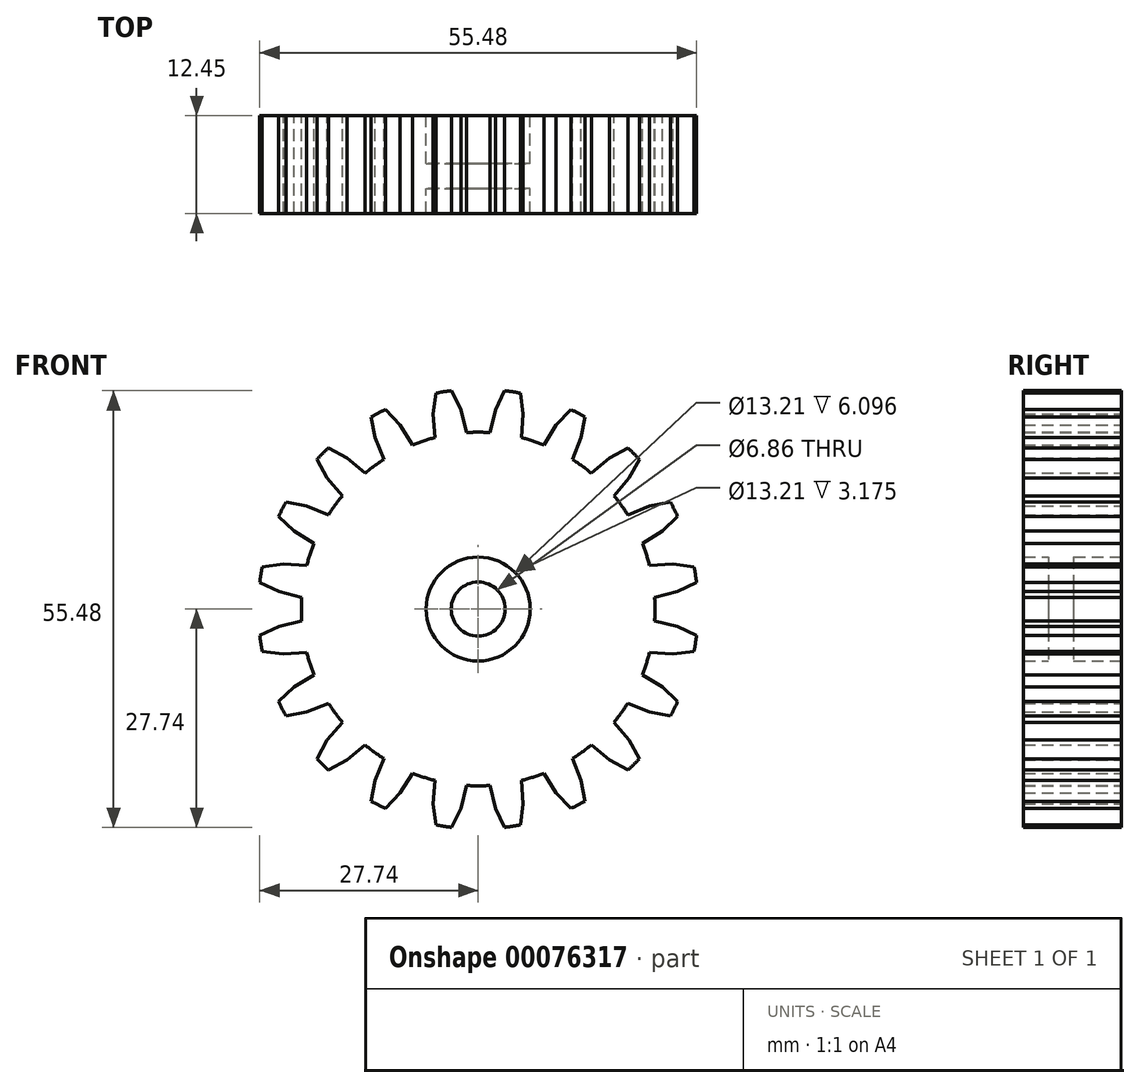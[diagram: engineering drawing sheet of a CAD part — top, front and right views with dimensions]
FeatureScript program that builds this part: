
annotation { "Feature Type Name" : "Feature", "Feature Type Description" : "" }
export const myFeature = defineFeature(function(context is Context, id is Id, definition is map)
    precondition{}
    {
        {
            var Q0;
            Q0=qCreatedBy(makeId("Top.planeOp"),FACE);
            var sketch = newSketch(context, id + "F0", { "sketchPlane" : qUnion([Q0])});
            skLineSegment(sketch, "E0", {"start": v(0, 6.35) * mm, "end": v(0, -6.35) * mm});
            skLineSegment(sketch, "E1", {"start": v(6.6, 6.35) * mm, "end": v(6.6, -6.35) * mm});
            skLineSegment(sketch, "E2", {"start": v(6.6, -6.35) * mm, "end": v(50.8, -6.35) * mm});
            skLineSegment(sketch, "E3", {"start": v(50.8, -6.35) * mm, "end": v(50.8, 6.35) * mm});
            skLineSegment(sketch, "E4", {"start": v(50.8, 6.35) * mm, "end": v(6.6, 6.35) * mm});
            skLineSegment(sketch, "E5", {"start": v(6.6, 0) * mm, "end": v(3.43, 0) * mm});
            skLineSegment(sketch, "E6", {"start": v(3.43, 0) * mm, "end": v(3.43, -3.18) * mm});
            skLineSegment(sketch, "E7", {"start": v(3.43, -3.18) * mm, "end": v(6.6, -3.18) * mm});
            skSolve(sketch);
        }
        {
            var Q0;
            Q0=makeQuery(id+"F0.imprint","IMPRINT",FACE,{"disambiguationData":[TD([[makeQuery(id+"F0.imprint","IMPRINT",EDGE,{"derivedFrom":sQuery(id+"F0.wireOp",EDGE,"3r0X1BRl-RbRB-vlo6-oPl6-QrHitKXkx0XH")}),1.0]])]});
            var Q1;
            Q1=makeQuery(id+"F0.imprint","IMPRINT",FACE,{"disambiguationData":[TD([[makeQuery(id+"F0.imprint","IMPRINT",EDGE,{"derivedFrom":sQuery(id+"F0.wireOp",EDGE,"E1")}),1.0]])]});
            var Q2;
            {var subQ4=sQuery(id+"F0.wireOp",EDGE,"VTUfDxQO-eAQO-8rXd-4OAK-vWdJqYTGuIOz");Q2=makeQuery(id+"F0.imprint","IMPRINT",FACE,{"disambiguationData":[TD([[makeQuery(id+"F0.imprint","IMPRINT",EDGE,{"derivedFrom":subQ4}),1.0]])]});}
            var Q3;
            {var subQ0=sQuery(id+"F0.wireOp",EDGE,"E5");Q3=makeQuery(id+"F0.imprint","IMPRINT",FACE,{"disambiguationData":[TD([[makeQuery(id+"F0.imprint","IMPRINT",EDGE,{"derivedFrom":subQ0}),1.0]])]});}
            var Q4;
            Q4=sQuery(id+"F0.wireOp",EDGE,"E0");
            revolve(context, id + "F1", {"entities" : qUnion([Q0, Q1, Q2, Q3]), "axis" : qUnion([Q4]), "revolveType" : RevolveType.FULL});
        }
        {
            var Q0;
            Q0=makeQuery(id+"F1.opRevolve","SWEPT_FACE",FACE,{"disambiguationData":[OSD([sQuery(id+"F0.wireOp",EDGE,"E4")])]});
            var sketch = newSketch(context, id + "F2", { "sketchPlane" : qUnion([Q0])});
            skCircle(sketch, "E8.0", {"center": v(0, 0) * mm, "radius": 50.8 * mm, "construction": true});
            skCircle(sketch, "E9", {"center": v(76.2, 0) * mm, "radius": 25.4 * mm, "construction": true});
            skCircle(sketch, "E10", {"center": v(0, 0) * mm, "radius": 53.34 * mm, "construction": true});
            skCircle(sketch, "E11", {"center": v(0, 0) * mm, "radius": 47.86 * mm, "construction": true});
            skLineSegment(sketch, "E12", {"start": v(-2.03, 47.82) * mm, "end": v(-1.78, 50.77) * mm});
            skLineSegment(sketch, "E13", {"start": v(-1.78, 50.77) * mm, "end": v(-1.02, 53.33) * mm});
            skLineSegment(sketch, "E14", {"start": v(2.03, 47.82) * mm, "end": v(1.78, 50.77) * mm});
            skLineSegment(sketch, "E15", {"start": v(1.78, 50.77) * mm, "end": v(1.02, 53.33) * mm});
            skCircle(sketch, "E16", {"center": v(76.2, 0) * mm, "radius": 27.94 * mm, "construction": true});
            skCircle(sketch, "E17", {"center": v(76.2, 0) * mm, "radius": 22.46 * mm, "construction": true});
            skLineSegment(sketch, "E18.1.0", {"start": v(-5.47, 47.55) * mm, "end": v(-6.19, 50.42) * mm});
            skLineSegment(sketch, "E18.1.1", {"start": v(-9.49, 46.91) * mm, "end": v(-9.7, 49.87) * mm});
            skLineSegment(sketch, "E18.1.2", {"start": v(-9.7, 49.87) * mm, "end": v(-9.35, 52.51) * mm});
            skLineSegment(sketch, "E18.1.3", {"start": v(-6.19, 50.42) * mm, "end": v(-7.34, 52.83) * mm});
            skLineSegment(sketch, "E18.2.0", {"start": v(-12.84, 46.1) * mm, "end": v(-14, 48.83) * mm});
            skLineSegment(sketch, "E18.2.1", {"start": v(-16.7, 44.85) * mm, "end": v(-17.38, 47.73) * mm});
            skLineSegment(sketch, "E18.2.2", {"start": v(-17.38, 47.73) * mm, "end": v(-17.45, 50.4) * mm});
            skLineSegment(sketch, "E18.2.3", {"start": v(-14, 48.83) * mm, "end": v(-15.51, 51.03) * mm});
            skLineSegment(sketch, "E18.3.0", {"start": v(-19.9, 43.53) * mm, "end": v(-21.46, 46.04) * mm});
            skLineSegment(sketch, "E18.3.1", {"start": v(-23.52, 41.68) * mm, "end": v(-24.63, 44.43) * mm});
            skLineSegment(sketch, "E18.3.2", {"start": v(-24.63, 44.43) * mm, "end": v(-25.12, 47.06) * mm});
            skLineSegment(sketch, "E18.3.3", {"start": v(-21.46, 46.04) * mm, "end": v(-23.3, 47.98) * mm});
            skLineSegment(sketch, "E18.4.0", {"start": v(-26.46, 39.88) * mm, "end": v(-28.4, 42.12) * mm});
            skLineSegment(sketch, "E18.4.1", {"start": v(-29.75, 37.5) * mm, "end": v(-31.28, 40.03) * mm});
            skLineSegment(sketch, "E18.4.2", {"start": v(-31.28, 40.03) * mm, "end": v(-32.17, 42.55) * mm});
            skLineSegment(sketch, "E18.4.3", {"start": v(-28.4, 42.12) * mm, "end": v(-30.52, 43.74) * mm});
            skLineSegment(sketch, "E18.5.0", {"start": v(-32.38, 35.25) * mm, "end": v(-34.64, 37.16) * mm});
            skLineSegment(sketch, "E18.5.1", {"start": v(-35.25, 32.38) * mm, "end": v(-37.16, 34.64) * mm});
            skLineSegment(sketch, "E18.5.2", {"start": v(-37.16, 34.64) * mm, "end": v(-38.43, 37) * mm});
            skLineSegment(sketch, "E18.5.3", {"start": v(-34.64, 37.16) * mm, "end": v(-37, 38.43) * mm});
            skLineSegment(sketch, "E18.6.0", {"start": v(-37.5, 29.75) * mm, "end": v(-40.03, 31.28) * mm});
            skLineSegment(sketch, "E18.6.1", {"start": v(-39.88, 26.46) * mm, "end": v(-42.12, 28.4) * mm});
            skLineSegment(sketch, "E18.6.2", {"start": v(-42.12, 28.4) * mm, "end": v(-43.74, 30.52) * mm});
            skLineSegment(sketch, "E18.6.3", {"start": v(-40.03, 31.28) * mm, "end": v(-42.55, 32.17) * mm});
            skLineSegment(sketch, "E18.7.0", {"start": v(-41.68, 23.52) * mm, "end": v(-44.43, 24.63) * mm});
            skLineSegment(sketch, "E18.7.1", {"start": v(-43.53, 19.9) * mm, "end": v(-46.04, 21.46) * mm});
            skLineSegment(sketch, "E18.7.2", {"start": v(-46.04, 21.46) * mm, "end": v(-47.98, 23.3) * mm});
            skLineSegment(sketch, "E18.7.3", {"start": v(-44.43, 24.63) * mm, "end": v(-47.06, 25.12) * mm});
            skLineSegment(sketch, "E18.8.0", {"start": v(-44.85, 16.7) * mm, "end": v(-47.73, 17.38) * mm});
            skLineSegment(sketch, "E18.8.1", {"start": v(-46.1, 12.84) * mm, "end": v(-48.83, 14) * mm});
            skLineSegment(sketch, "E18.8.2", {"start": v(-48.83, 14) * mm, "end": v(-51.03, 15.51) * mm});
            skLineSegment(sketch, "E18.8.3", {"start": v(-47.73, 17.38) * mm, "end": v(-50.4, 17.45) * mm});
            skLineSegment(sketch, "E18.9.0", {"start": v(-46.91, 9.49) * mm, "end": v(-49.87, 9.7) * mm});
            skLineSegment(sketch, "E18.9.1", {"start": v(-47.55, 5.47) * mm, "end": v(-50.42, 6.19) * mm});
            skLineSegment(sketch, "E18.9.2", {"start": v(-50.42, 6.19) * mm, "end": v(-52.83, 7.34) * mm});
            skLineSegment(sketch, "E18.9.3", {"start": v(-49.87, 9.7) * mm, "end": v(-52.51, 9.35) * mm});
            skLineSegment(sketch, "E18.10.0", {"start": v(-47.82, 2.03) * mm, "end": v(-50.77, 1.78) * mm});
            skLineSegment(sketch, "E18.10.1", {"start": v(-47.82, -2.03) * mm, "end": v(-50.77, -1.78) * mm});
            skLineSegment(sketch, "E18.10.2", {"start": v(-50.77, -1.78) * mm, "end": v(-53.33, -1.02) * mm});
            skLineSegment(sketch, "E18.10.3", {"start": v(-50.77, 1.78) * mm, "end": v(-53.33, 1.02) * mm});
            skLineSegment(sketch, "E18.11.0", {"start": v(-47.55, -5.47) * mm, "end": v(-50.42, -6.19) * mm});
            skLineSegment(sketch, "E18.11.1", {"start": v(-46.91, -9.49) * mm, "end": v(-49.87, -9.7) * mm});
            skLineSegment(sketch, "E18.11.2", {"start": v(-49.87, -9.7) * mm, "end": v(-52.51, -9.35) * mm});
            skLineSegment(sketch, "E18.11.3", {"start": v(-50.42, -6.19) * mm, "end": v(-52.83, -7.34) * mm});
            skLineSegment(sketch, "E18.12.0", {"start": v(-46.1, -12.84) * mm, "end": v(-48.83, -14) * mm});
            skLineSegment(sketch, "E18.12.1", {"start": v(-44.85, -16.7) * mm, "end": v(-47.73, -17.38) * mm});
            skLineSegment(sketch, "E18.12.2", {"start": v(-47.73, -17.38) * mm, "end": v(-50.4, -17.45) * mm});
            skLineSegment(sketch, "E18.12.3", {"start": v(-48.83, -14) * mm, "end": v(-51.03, -15.51) * mm});
            skLineSegment(sketch, "E18.13.0", {"start": v(-43.53, -19.9) * mm, "end": v(-46.04, -21.46) * mm});
            skLineSegment(sketch, "E18.13.1", {"start": v(-41.68, -23.52) * mm, "end": v(-44.43, -24.63) * mm});
            skLineSegment(sketch, "E18.13.2", {"start": v(-44.43, -24.63) * mm, "end": v(-47.06, -25.12) * mm});
            skLineSegment(sketch, "E18.13.3", {"start": v(-46.04, -21.46) * mm, "end": v(-47.98, -23.3) * mm});
            skLineSegment(sketch, "E18.14.0", {"start": v(-39.88, -26.46) * mm, "end": v(-42.12, -28.4) * mm});
            skLineSegment(sketch, "E18.14.1", {"start": v(-37.5, -29.75) * mm, "end": v(-40.03, -31.28) * mm});
            skLineSegment(sketch, "E18.14.2", {"start": v(-40.03, -31.28) * mm, "end": v(-42.55, -32.17) * mm});
            skLineSegment(sketch, "E18.14.3", {"start": v(-42.12, -28.4) * mm, "end": v(-43.74, -30.52) * mm});
            skLineSegment(sketch, "E18.15.0", {"start": v(-35.25, -32.38) * mm, "end": v(-37.16, -34.64) * mm});
            skLineSegment(sketch, "E18.15.1", {"start": v(-32.38, -35.25) * mm, "end": v(-34.64, -37.16) * mm});
            skLineSegment(sketch, "E18.15.2", {"start": v(-34.64, -37.16) * mm, "end": v(-37, -38.43) * mm});
            skLineSegment(sketch, "E18.15.3", {"start": v(-37.16, -34.64) * mm, "end": v(-38.43, -37) * mm});
            skLineSegment(sketch, "E18.16.0", {"start": v(-29.75, -37.5) * mm, "end": v(-31.28, -40.03) * mm});
            skLineSegment(sketch, "E18.16.1", {"start": v(-26.46, -39.88) * mm, "end": v(-28.4, -42.12) * mm});
            skLineSegment(sketch, "E18.16.2", {"start": v(-28.4, -42.12) * mm, "end": v(-30.52, -43.74) * mm});
            skLineSegment(sketch, "E18.16.3", {"start": v(-31.28, -40.03) * mm, "end": v(-32.17, -42.55) * mm});
            skLineSegment(sketch, "E18.17.0", {"start": v(-23.52, -41.68) * mm, "end": v(-24.63, -44.43) * mm});
            skLineSegment(sketch, "E18.17.1", {"start": v(-19.9, -43.53) * mm, "end": v(-21.46, -46.04) * mm});
            skLineSegment(sketch, "E18.17.2", {"start": v(-21.46, -46.04) * mm, "end": v(-23.3, -47.98) * mm});
            skLineSegment(sketch, "E18.17.3", {"start": v(-24.63, -44.43) * mm, "end": v(-25.12, -47.06) * mm});
            skLineSegment(sketch, "E18.18.0", {"start": v(-16.7, -44.85) * mm, "end": v(-17.38, -47.73) * mm});
            skLineSegment(sketch, "E18.18.1", {"start": v(-12.84, -46.1) * mm, "end": v(-14, -48.83) * mm});
            skLineSegment(sketch, "E18.18.2", {"start": v(-14, -48.83) * mm, "end": v(-15.51, -51.03) * mm});
            skLineSegment(sketch, "E18.18.3", {"start": v(-17.38, -47.73) * mm, "end": v(-17.45, -50.4) * mm});
            skLineSegment(sketch, "E18.19.0", {"start": v(-9.49, -46.91) * mm, "end": v(-9.7, -49.87) * mm});
            skLineSegment(sketch, "E18.19.1", {"start": v(-5.47, -47.55) * mm, "end": v(-6.19, -50.42) * mm});
            skLineSegment(sketch, "E18.19.2", {"start": v(-6.19, -50.42) * mm, "end": v(-7.34, -52.83) * mm});
            skLineSegment(sketch, "E18.19.3", {"start": v(-9.7, -49.87) * mm, "end": v(-9.35, -52.51) * mm});
            skLineSegment(sketch, "E18.20.0", {"start": v(-2.03, -47.82) * mm, "end": v(-1.78, -50.77) * mm});
            skLineSegment(sketch, "E18.20.1", {"start": v(2.03, -47.82) * mm, "end": v(1.78, -50.77) * mm});
            skLineSegment(sketch, "E18.20.2", {"start": v(1.78, -50.77) * mm, "end": v(1.02, -53.33) * mm});
            skLineSegment(sketch, "E18.20.3", {"start": v(-1.78, -50.77) * mm, "end": v(-1.02, -53.33) * mm});
            skLineSegment(sketch, "E18.21.0", {"start": v(5.47, -47.55) * mm, "end": v(6.19, -50.42) * mm});
            skLineSegment(sketch, "E18.21.1", {"start": v(9.49, -46.91) * mm, "end": v(9.7, -49.87) * mm});
            skLineSegment(sketch, "E18.21.2", {"start": v(9.7, -49.87) * mm, "end": v(9.35, -52.51) * mm});
            skLineSegment(sketch, "E18.21.3", {"start": v(6.19, -50.42) * mm, "end": v(7.34, -52.83) * mm});
            skLineSegment(sketch, "E18.22.0", {"start": v(12.84, -46.1) * mm, "end": v(14, -48.83) * mm});
            skLineSegment(sketch, "E18.22.1", {"start": v(16.7, -44.85) * mm, "end": v(17.38, -47.73) * mm});
            skLineSegment(sketch, "E18.22.2", {"start": v(17.38, -47.73) * mm, "end": v(17.45, -50.4) * mm});
            skLineSegment(sketch, "E18.22.3", {"start": v(14, -48.83) * mm, "end": v(15.51, -51.03) * mm});
            skLineSegment(sketch, "E18.23.0", {"start": v(19.9, -43.53) * mm, "end": v(21.46, -46.04) * mm});
            skLineSegment(sketch, "E18.23.1", {"start": v(23.52, -41.68) * mm, "end": v(24.63, -44.43) * mm});
            skLineSegment(sketch, "E18.23.2", {"start": v(24.63, -44.43) * mm, "end": v(25.12, -47.06) * mm});
            skLineSegment(sketch, "E18.23.3", {"start": v(21.46, -46.04) * mm, "end": v(23.3, -47.98) * mm});
            skLineSegment(sketch, "E18.24.0", {"start": v(26.46, -39.88) * mm, "end": v(28.4, -42.12) * mm});
            skLineSegment(sketch, "E18.24.1", {"start": v(29.75, -37.5) * mm, "end": v(31.28, -40.03) * mm});
            skLineSegment(sketch, "E18.24.2", {"start": v(31.28, -40.03) * mm, "end": v(32.17, -42.55) * mm});
            skLineSegment(sketch, "E18.24.3", {"start": v(28.4, -42.12) * mm, "end": v(30.52, -43.74) * mm});
            skLineSegment(sketch, "E18.25.0", {"start": v(32.38, -35.25) * mm, "end": v(34.64, -37.16) * mm});
            skLineSegment(sketch, "E18.25.1", {"start": v(35.25, -32.38) * mm, "end": v(37.16, -34.64) * mm});
            skLineSegment(sketch, "E18.25.2", {"start": v(37.16, -34.64) * mm, "end": v(38.43, -37) * mm});
            skLineSegment(sketch, "E18.25.3", {"start": v(34.64, -37.16) * mm, "end": v(37, -38.43) * mm});
            skLineSegment(sketch, "E18.26.0", {"start": v(37.5, -29.75) * mm, "end": v(40.03, -31.28) * mm});
            skLineSegment(sketch, "E18.26.1", {"start": v(39.88, -26.46) * mm, "end": v(42.12, -28.4) * mm});
            skLineSegment(sketch, "E18.26.2", {"start": v(42.12, -28.4) * mm, "end": v(43.74, -30.52) * mm});
            skLineSegment(sketch, "E18.26.3", {"start": v(40.03, -31.28) * mm, "end": v(42.55, -32.17) * mm});
            skLineSegment(sketch, "E18.27.0", {"start": v(41.68, -23.52) * mm, "end": v(44.43, -24.63) * mm});
            skLineSegment(sketch, "E18.27.1", {"start": v(43.53, -19.9) * mm, "end": v(46.04, -21.46) * mm});
            skLineSegment(sketch, "E18.27.2", {"start": v(46.04, -21.46) * mm, "end": v(47.98, -23.3) * mm});
            skLineSegment(sketch, "E18.27.3", {"start": v(44.43, -24.63) * mm, "end": v(47.06, -25.12) * mm});
            skLineSegment(sketch, "E18.28.0", {"start": v(44.85, -16.7) * mm, "end": v(47.73, -17.38) * mm});
            skLineSegment(sketch, "E18.28.1", {"start": v(46.1, -12.84) * mm, "end": v(48.83, -14) * mm});
            skLineSegment(sketch, "E18.28.2", {"start": v(48.83, -14) * mm, "end": v(51.03, -15.51) * mm});
            skLineSegment(sketch, "E18.28.3", {"start": v(47.73, -17.38) * mm, "end": v(50.4, -17.45) * mm});
            skLineSegment(sketch, "E18.29.0", {"start": v(46.91, -9.49) * mm, "end": v(49.87, -9.7) * mm});
            skLineSegment(sketch, "E18.29.1", {"start": v(47.55, -5.47) * mm, "end": v(50.42, -6.19) * mm});
            skLineSegment(sketch, "E18.29.2", {"start": v(50.42, -6.19) * mm, "end": v(52.83, -7.34) * mm});
            skLineSegment(sketch, "E18.29.3", {"start": v(49.87, -9.7) * mm, "end": v(52.51, -9.35) * mm});
            skLineSegment(sketch, "E18.30.0", {"start": v(47.82, -2.03) * mm, "end": v(50.77, -1.78) * mm});
            skLineSegment(sketch, "E18.30.1", {"start": v(47.82, 2.03) * mm, "end": v(50.77, 1.78) * mm});
            skLineSegment(sketch, "E18.30.2", {"start": v(50.77, 1.78) * mm, "end": v(53.33, 1.02) * mm});
            skLineSegment(sketch, "E18.30.3", {"start": v(50.77, -1.78) * mm, "end": v(53.33, -1.02) * mm});
            skLineSegment(sketch, "E18.31.0", {"start": v(47.55, 5.47) * mm, "end": v(50.42, 6.19) * mm});
            skLineSegment(sketch, "E18.31.1", {"start": v(46.91, 9.49) * mm, "end": v(49.87, 9.7) * mm});
            skLineSegment(sketch, "E18.31.2", {"start": v(49.87, 9.7) * mm, "end": v(52.51, 9.35) * mm});
            skLineSegment(sketch, "E18.31.3", {"start": v(50.42, 6.19) * mm, "end": v(52.83, 7.34) * mm});
            skLineSegment(sketch, "E18.32.0", {"start": v(46.1, 12.84) * mm, "end": v(48.83, 14) * mm});
            skLineSegment(sketch, "E18.32.1", {"start": v(44.85, 16.7) * mm, "end": v(47.73, 17.38) * mm});
            skLineSegment(sketch, "E18.32.2", {"start": v(47.73, 17.38) * mm, "end": v(50.4, 17.45) * mm});
            skLineSegment(sketch, "E18.32.3", {"start": v(48.83, 14) * mm, "end": v(51.03, 15.51) * mm});
            skLineSegment(sketch, "E18.33.0", {"start": v(43.53, 19.9) * mm, "end": v(46.04, 21.46) * mm});
            skLineSegment(sketch, "E18.33.1", {"start": v(41.68, 23.52) * mm, "end": v(44.43, 24.63) * mm});
            skLineSegment(sketch, "E18.33.2", {"start": v(44.43, 24.63) * mm, "end": v(47.06, 25.12) * mm});
            skLineSegment(sketch, "E18.33.3", {"start": v(46.04, 21.46) * mm, "end": v(47.98, 23.3) * mm});
            skLineSegment(sketch, "E18.34.0", {"start": v(39.88, 26.46) * mm, "end": v(42.12, 28.4) * mm});
            skLineSegment(sketch, "E18.34.1", {"start": v(37.5, 29.75) * mm, "end": v(40.03, 31.28) * mm});
            skLineSegment(sketch, "E18.34.2", {"start": v(40.03, 31.28) * mm, "end": v(42.55, 32.17) * mm});
            skLineSegment(sketch, "E18.34.3", {"start": v(42.12, 28.4) * mm, "end": v(43.74, 30.52) * mm});
            skLineSegment(sketch, "E18.35.0", {"start": v(35.25, 32.38) * mm, "end": v(37.16, 34.64) * mm});
            skLineSegment(sketch, "E18.35.1", {"start": v(32.38, 35.25) * mm, "end": v(34.64, 37.16) * mm});
            skLineSegment(sketch, "E18.35.2", {"start": v(34.64, 37.16) * mm, "end": v(37, 38.43) * mm});
            skLineSegment(sketch, "E18.35.3", {"start": v(37.16, 34.64) * mm, "end": v(38.43, 37) * mm});
            skLineSegment(sketch, "E18.36.0", {"start": v(29.75, 37.5) * mm, "end": v(31.28, 40.03) * mm});
            skLineSegment(sketch, "E18.36.1", {"start": v(26.46, 39.88) * mm, "end": v(28.4, 42.12) * mm});
            skLineSegment(sketch, "E18.36.2", {"start": v(28.4, 42.12) * mm, "end": v(30.52, 43.74) * mm});
            skLineSegment(sketch, "E18.36.3", {"start": v(31.28, 40.03) * mm, "end": v(32.17, 42.55) * mm});
            skLineSegment(sketch, "E18.37.0", {"start": v(23.52, 41.68) * mm, "end": v(24.63, 44.43) * mm});
            skLineSegment(sketch, "E18.37.1", {"start": v(19.9, 43.53) * mm, "end": v(21.46, 46.04) * mm});
            skLineSegment(sketch, "E18.37.2", {"start": v(21.46, 46.04) * mm, "end": v(23.3, 47.98) * mm});
            skLineSegment(sketch, "E18.37.3", {"start": v(24.63, 44.43) * mm, "end": v(25.12, 47.06) * mm});
            skLineSegment(sketch, "E18.38.0", {"start": v(16.7, 44.85) * mm, "end": v(17.38, 47.73) * mm});
            skLineSegment(sketch, "E18.38.1", {"start": v(12.84, 46.1) * mm, "end": v(14, 48.83) * mm});
            skLineSegment(sketch, "E18.38.2", {"start": v(14, 48.83) * mm, "end": v(15.51, 51.03) * mm});
            skLineSegment(sketch, "E18.38.3", {"start": v(17.38, 47.73) * mm, "end": v(17.45, 50.4) * mm});
            skLineSegment(sketch, "E18.39.0", {"start": v(9.49, 46.91) * mm, "end": v(9.7, 49.87) * mm});
            skLineSegment(sketch, "E18.39.1", {"start": v(5.47, 47.55) * mm, "end": v(6.19, 50.42) * mm});
            skLineSegment(sketch, "E18.39.2", {"start": v(6.19, 50.42) * mm, "end": v(7.34, 52.83) * mm});
            skLineSegment(sketch, "E18.39.3", {"start": v(9.7, 49.87) * mm, "end": v(9.35, 52.51) * mm});
            skLineSegment(sketch, "E19", {"start": v(77.7, 22.41) * mm, "end": v(78.4, 25.3) * mm});
            skLineSegment(sketch, "E20", {"start": v(78.4, 25.3) * mm, "end": v(79.56, 27.74) * mm});
            skLineSegment(sketch, "E21", {"start": v(81.7, 21.78) * mm, "end": v(81.92, 24.75) * mm});
            skLineSegment(sketch, "E22", {"start": v(81.92, 24.75) * mm, "end": v(81.57, 27.42) * mm});
            skLineSegment(sketch, "E23", {"start": v(76.2, 0) * mm, "end": v(79.71, 22.18) * mm});
            skLineSegment(sketch, "E24", {"start": v(76.2, 0) * mm, "end": v(76.2, 7.1) * mm});
            skLineSegment(sketch, "E25.1.0", {"start": v(74.7, 22.41) * mm, "end": v(74, 25.3) * mm});
            skLineSegment(sketch, "E25.1.1", {"start": v(74, 25.3) * mm, "end": v(72.84, 27.74) * mm});
            skLineSegment(sketch, "E25.1.2", {"start": v(70.48, 24.75) * mm, "end": v(70.83, 27.42) * mm});
            skLineSegment(sketch, "E25.1.3", {"start": v(70.7, 21.78) * mm, "end": v(70.48, 24.75) * mm});
            skLineSegment(sketch, "E25.2.0", {"start": v(67.86, 20.85) * mm, "end": v(66.28, 23.38) * mm});
            skLineSegment(sketch, "E25.2.1", {"start": v(66.28, 23.38) * mm, "end": v(64.43, 25.34) * mm});
            skLineSegment(sketch, "E25.2.2", {"start": v(63.11, 21.77) * mm, "end": v(62.62, 24.42) * mm});
            skLineSegment(sketch, "E25.2.3", {"start": v(64.23, 19) * mm, "end": v(63.11, 21.77) * mm});
            skLineSegment(sketch, "E25.3.0", {"start": v(61.82, 17.25) * mm, "end": v(59.54, 19.17) * mm});
            skLineSegment(sketch, "E25.3.1", {"start": v(59.54, 19.17) * mm, "end": v(57.17, 20.46) * mm});
            skLineSegment(sketch, "E25.3.2", {"start": v(57.03, 16.66) * mm, "end": v(55.74, 19.03) * mm});
            skLineSegment(sketch, "E25.3.3", {"start": v(58.95, 14.38) * mm, "end": v(57.03, 16.66) * mm});
            skLineSegment(sketch, "E25.4.0", {"start": v(57.2, 11.97) * mm, "end": v(54.43, 13.09) * mm});
            skLineSegment(sketch, "E25.4.1", {"start": v(54.43, 13.09) * mm, "end": v(51.78, 13.58) * mm});
            skLineSegment(sketch, "E25.4.2", {"start": v(52.82, 9.92) * mm, "end": v(50.86, 11.77) * mm});
            skLineSegment(sketch, "E25.4.3", {"start": v(55.35, 8.34) * mm, "end": v(52.82, 9.92) * mm});
            skLineSegment(sketch, "E25.5.0", {"start": v(54.42, 5.5) * mm, "end": v(51.45, 5.72) * mm});
            skLineSegment(sketch, "E25.5.1", {"start": v(51.45, 5.72) * mm, "end": v(48.78, 5.37) * mm});
            skLineSegment(sketch, "E25.5.2", {"start": v(50.9, 2.2) * mm, "end": v(48.46, 3.36) * mm});
            skLineSegment(sketch, "E25.5.3", {"start": v(53.79, 1.5) * mm, "end": v(50.9, 2.2) * mm});
            skLineSegment(sketch, "E25.6.0", {"start": v(53.79, -1.5) * mm, "end": v(50.9, -2.2) * mm});
            skLineSegment(sketch, "E25.6.1", {"start": v(50.9, -2.2) * mm, "end": v(48.46, -3.36) * mm});
            skLineSegment(sketch, "E25.6.2", {"start": v(51.45, -5.72) * mm, "end": v(48.78, -5.37) * mm});
            skLineSegment(sketch, "E25.6.3", {"start": v(54.42, -5.5) * mm, "end": v(51.45, -5.72) * mm});
            skLineSegment(sketch, "E25.7.0", {"start": v(55.35, -8.34) * mm, "end": v(52.82, -9.92) * mm});
            skLineSegment(sketch, "E25.7.1", {"start": v(52.82, -9.92) * mm, "end": v(50.86, -11.77) * mm});
            skLineSegment(sketch, "E25.7.2", {"start": v(54.43, -13.09) * mm, "end": v(51.78, -13.58) * mm});
            skLineSegment(sketch, "E25.7.3", {"start": v(57.2, -11.97) * mm, "end": v(54.43, -13.09) * mm});
            skLineSegment(sketch, "E25.8.0", {"start": v(58.95, -14.38) * mm, "end": v(57.03, -16.66) * mm});
            skLineSegment(sketch, "E25.8.1", {"start": v(57.03, -16.66) * mm, "end": v(55.74, -19.03) * mm});
            skLineSegment(sketch, "E25.8.2", {"start": v(59.54, -19.17) * mm, "end": v(57.17, -20.46) * mm});
            skLineSegment(sketch, "E25.8.3", {"start": v(61.82, -17.25) * mm, "end": v(59.54, -19.17) * mm});
            skLineSegment(sketch, "E25.9.0", {"start": v(64.23, -19) * mm, "end": v(63.11, -21.77) * mm});
            skLineSegment(sketch, "E25.9.1", {"start": v(63.11, -21.77) * mm, "end": v(62.62, -24.42) * mm});
            skLineSegment(sketch, "E25.9.2", {"start": v(66.28, -23.38) * mm, "end": v(64.43, -25.34) * mm});
            skLineSegment(sketch, "E25.9.3", {"start": v(67.86, -20.85) * mm, "end": v(66.28, -23.38) * mm});
            skLineSegment(sketch, "E25.10.0", {"start": v(70.7, -21.78) * mm, "end": v(70.48, -24.75) * mm});
            skLineSegment(sketch, "E25.10.1", {"start": v(70.48, -24.75) * mm, "end": v(70.83, -27.42) * mm});
            skLineSegment(sketch, "E25.10.2", {"start": v(74, -25.3) * mm, "end": v(72.84, -27.74) * mm});
            skLineSegment(sketch, "E25.10.3", {"start": v(74.7, -22.41) * mm, "end": v(74, -25.3) * mm});
            skLineSegment(sketch, "E25.11.0", {"start": v(77.7, -22.41) * mm, "end": v(78.4, -25.3) * mm});
            skLineSegment(sketch, "E25.11.1", {"start": v(78.4, -25.3) * mm, "end": v(79.56, -27.74) * mm});
            skLineSegment(sketch, "E25.11.2", {"start": v(81.92, -24.75) * mm, "end": v(81.57, -27.42) * mm});
            skLineSegment(sketch, "E25.11.3", {"start": v(81.7, -21.78) * mm, "end": v(81.92, -24.75) * mm});
            skLineSegment(sketch, "E25.12.0", {"start": v(84.54, -20.85) * mm, "end": v(86.12, -23.38) * mm});
            skLineSegment(sketch, "E25.12.1", {"start": v(86.12, -23.38) * mm, "end": v(87.97, -25.34) * mm});
            skLineSegment(sketch, "E25.12.2", {"start": v(89.29, -21.77) * mm, "end": v(89.78, -24.42) * mm});
            skLineSegment(sketch, "E25.12.3", {"start": v(88.17, -19) * mm, "end": v(89.29, -21.77) * mm});
            skLineSegment(sketch, "E25.13.0", {"start": v(90.58, -17.25) * mm, "end": v(92.86, -19.17) * mm});
            skLineSegment(sketch, "E25.13.1", {"start": v(92.86, -19.17) * mm, "end": v(95.23, -20.46) * mm});
            skLineSegment(sketch, "E25.13.2", {"start": v(95.37, -16.66) * mm, "end": v(96.66, -19.03) * mm});
            skLineSegment(sketch, "E25.13.3", {"start": v(93.45, -14.38) * mm, "end": v(95.37, -16.66) * mm});
            skLineSegment(sketch, "E25.14.0", {"start": v(95.2, -11.97) * mm, "end": v(97.97, -13.09) * mm});
            skLineSegment(sketch, "E25.14.1", {"start": v(97.97, -13.09) * mm, "end": v(100.62, -13.58) * mm});
            skLineSegment(sketch, "E25.14.2", {"start": v(99.58, -9.92) * mm, "end": v(101.54, -11.77) * mm});
            skLineSegment(sketch, "E25.14.3", {"start": v(97.05, -8.34) * mm, "end": v(99.58, -9.92) * mm});
            skLineSegment(sketch, "E25.15.0", {"start": v(97.98, -5.5) * mm, "end": v(100.95, -5.72) * mm});
            skLineSegment(sketch, "E25.15.1", {"start": v(100.95, -5.72) * mm, "end": v(103.62, -5.37) * mm});
            skLineSegment(sketch, "E25.15.2", {"start": v(101.5, -2.2) * mm, "end": v(103.94, -3.36) * mm});
            skLineSegment(sketch, "E25.15.3", {"start": v(98.61, -1.5) * mm, "end": v(101.5, -2.2) * mm});
            skLineSegment(sketch, "E25.16.0", {"start": v(98.61, 1.5) * mm, "end": v(101.5, 2.2) * mm});
            skLineSegment(sketch, "E25.16.1", {"start": v(101.5, 2.2) * mm, "end": v(103.94, 3.36) * mm});
            skLineSegment(sketch, "E25.16.2", {"start": v(100.95, 5.72) * mm, "end": v(103.62, 5.37) * mm});
            skLineSegment(sketch, "E25.16.3", {"start": v(97.98, 5.5) * mm, "end": v(100.95, 5.72) * mm});
            skLineSegment(sketch, "E25.17.0", {"start": v(97.05, 8.34) * mm, "end": v(99.58, 9.92) * mm});
            skLineSegment(sketch, "E25.17.1", {"start": v(99.58, 9.92) * mm, "end": v(101.54, 11.77) * mm});
            skLineSegment(sketch, "E25.17.2", {"start": v(97.97, 13.09) * mm, "end": v(100.62, 13.58) * mm});
            skLineSegment(sketch, "E25.17.3", {"start": v(95.2, 11.97) * mm, "end": v(97.97, 13.09) * mm});
            skLineSegment(sketch, "E25.18.0", {"start": v(93.45, 14.38) * mm, "end": v(95.37, 16.66) * mm});
            skLineSegment(sketch, "E25.18.1", {"start": v(95.37, 16.66) * mm, "end": v(96.66, 19.03) * mm});
            skLineSegment(sketch, "E25.18.2", {"start": v(92.86, 19.17) * mm, "end": v(95.23, 20.46) * mm});
            skLineSegment(sketch, "E25.18.3", {"start": v(90.58, 17.25) * mm, "end": v(92.86, 19.17) * mm});
            skLineSegment(sketch, "E25.19.0", {"start": v(88.17, 19) * mm, "end": v(89.29, 21.77) * mm});
            skLineSegment(sketch, "E25.19.1", {"start": v(89.29, 21.77) * mm, "end": v(89.78, 24.42) * mm});
            skLineSegment(sketch, "E25.19.2", {"start": v(86.12, 23.38) * mm, "end": v(87.97, 25.34) * mm});
            skLineSegment(sketch, "E25.19.3", {"start": v(84.54, 20.85) * mm, "end": v(86.12, 23.38) * mm});
            skCircle(sketch, "E26", {"center": v(0, 0) * mm, "radius": 25.4 * mm, "construction": true});
            skCircle(sketch, "E27", {"center": v(0, 0) * mm, "radius": 27.94 * mm});
            skCircle(sketch, "E28", {"center": v(0, 0) * mm, "radius": 22.46 * mm});
            skLineSegment(sketch, "E29", {"start": v(1.5, 22.41) * mm, "end": v(2.2, 25.3) * mm});
            skLineSegment(sketch, "E30", {"start": v(2.2, 25.3) * mm, "end": v(3.36, 27.74) * mm});
            skLineSegment(sketch, "E31", {"start": v(5.5, 21.78) * mm, "end": v(5.72, 24.75) * mm});
            skLineSegment(sketch, "E32", {"start": v(5.72, 24.75) * mm, "end": v(5.37, 27.42) * mm});
            skLineSegment(sketch, "E33", {"start": v(0, 0) * mm, "end": v(3.51, 22.18) * mm});
            skLineSegment(sketch, "E34", {"start": v(0, -50.56) * mm, "end": v(0, 0) * mm});
            skLineSegment(sketch, "E35.1.0", {"start": v(-1.5, 22.41) * mm, "end": v(-2.2, 25.3) * mm});
            skLineSegment(sketch, "E35.1.1", {"start": v(-2.2, 25.3) * mm, "end": v(-3.36, 27.74) * mm});
            skLineSegment(sketch, "E35.1.2", {"start": v(-5.72, 24.75) * mm, "end": v(-5.37, 27.42) * mm});
            skLineSegment(sketch, "E35.1.3", {"start": v(-5.5, 21.78) * mm, "end": v(-5.72, 24.75) * mm});
            skLineSegment(sketch, "E35.2.0", {"start": v(-8.34, 20.85) * mm, "end": v(-9.92, 23.38) * mm});
            skLineSegment(sketch, "E35.2.1", {"start": v(-9.92, 23.38) * mm, "end": v(-11.77, 25.34) * mm});
            skLineSegment(sketch, "E35.2.2", {"start": v(-13.09, 21.77) * mm, "end": v(-13.58, 24.42) * mm});
            skLineSegment(sketch, "E35.2.3", {"start": v(-11.97, 19) * mm, "end": v(-13.09, 21.77) * mm});
            skLineSegment(sketch, "E35.3.0", {"start": v(-14.38, 17.25) * mm, "end": v(-16.66, 19.17) * mm});
            skLineSegment(sketch, "E35.3.1", {"start": v(-16.66, 19.17) * mm, "end": v(-19.03, 20.46) * mm});
            skLineSegment(sketch, "E35.3.2", {"start": v(-19.17, 16.66) * mm, "end": v(-20.46, 19.03) * mm});
            skLineSegment(sketch, "E35.3.3", {"start": v(-17.25, 14.38) * mm, "end": v(-19.17, 16.66) * mm});
            skLineSegment(sketch, "E35.4.0", {"start": v(-19, 11.97) * mm, "end": v(-21.77, 13.09) * mm});
            skLineSegment(sketch, "E35.4.1", {"start": v(-21.77, 13.09) * mm, "end": v(-24.42, 13.58) * mm});
            skLineSegment(sketch, "E35.4.2", {"start": v(-23.38, 9.92) * mm, "end": v(-25.34, 11.77) * mm});
            skLineSegment(sketch, "E35.4.3", {"start": v(-20.85, 8.34) * mm, "end": v(-23.38, 9.92) * mm});
            skLineSegment(sketch, "E35.5.0", {"start": v(-21.78, 5.5) * mm, "end": v(-24.75, 5.72) * mm});
            skLineSegment(sketch, "E35.5.1", {"start": v(-24.75, 5.72) * mm, "end": v(-27.42, 5.37) * mm});
            skLineSegment(sketch, "E35.5.2", {"start": v(-25.3, 2.2) * mm, "end": v(-27.74, 3.36) * mm});
            skLineSegment(sketch, "E35.5.3", {"start": v(-22.41, 1.5) * mm, "end": v(-25.3, 2.2) * mm});
            skLineSegment(sketch, "E35.6.0", {"start": v(-22.41, -1.5) * mm, "end": v(-25.3, -2.2) * mm});
            skLineSegment(sketch, "E35.6.1", {"start": v(-25.3, -2.2) * mm, "end": v(-27.74, -3.36) * mm});
            skLineSegment(sketch, "E35.6.2", {"start": v(-24.75, -5.72) * mm, "end": v(-27.42, -5.37) * mm});
            skLineSegment(sketch, "E35.6.3", {"start": v(-21.78, -5.5) * mm, "end": v(-24.75, -5.72) * mm});
            skLineSegment(sketch, "E35.7.0", {"start": v(-20.85, -8.34) * mm, "end": v(-23.38, -9.92) * mm});
            skLineSegment(sketch, "E35.7.1", {"start": v(-23.38, -9.92) * mm, "end": v(-25.34, -11.77) * mm});
            skLineSegment(sketch, "E35.7.2", {"start": v(-21.77, -13.09) * mm, "end": v(-24.42, -13.58) * mm});
            skLineSegment(sketch, "E35.7.3", {"start": v(-19, -11.97) * mm, "end": v(-21.77, -13.09) * mm});
            skLineSegment(sketch, "E35.8.0", {"start": v(-17.25, -14.38) * mm, "end": v(-19.17, -16.66) * mm});
            skLineSegment(sketch, "E35.8.1", {"start": v(-19.17, -16.66) * mm, "end": v(-20.46, -19.03) * mm});
            skLineSegment(sketch, "E35.8.2", {"start": v(-16.66, -19.17) * mm, "end": v(-19.03, -20.46) * mm});
            skLineSegment(sketch, "E35.8.3", {"start": v(-14.38, -17.25) * mm, "end": v(-16.66, -19.17) * mm});
            skLineSegment(sketch, "E35.9.0", {"start": v(-11.97, -19) * mm, "end": v(-13.09, -21.77) * mm});
            skLineSegment(sketch, "E35.9.1", {"start": v(-13.09, -21.77) * mm, "end": v(-13.58, -24.42) * mm});
            skLineSegment(sketch, "E35.9.2", {"start": v(-9.92, -23.38) * mm, "end": v(-11.77, -25.34) * mm});
            skLineSegment(sketch, "E35.9.3", {"start": v(-8.34, -20.85) * mm, "end": v(-9.92, -23.38) * mm});
            skLineSegment(sketch, "E35.10.0", {"start": v(-5.5, -21.78) * mm, "end": v(-5.72, -24.75) * mm});
            skLineSegment(sketch, "E35.10.1", {"start": v(-5.72, -24.75) * mm, "end": v(-5.37, -27.42) * mm});
            skLineSegment(sketch, "E35.10.2", {"start": v(-2.2, -25.3) * mm, "end": v(-3.36, -27.74) * mm});
            skLineSegment(sketch, "E35.10.3", {"start": v(-1.5, -22.41) * mm, "end": v(-2.2, -25.3) * mm});
            skLineSegment(sketch, "E35.11.0", {"start": v(1.5, -22.41) * mm, "end": v(2.2, -25.3) * mm});
            skLineSegment(sketch, "E35.11.1", {"start": v(2.2, -25.3) * mm, "end": v(3.36, -27.74) * mm});
            skLineSegment(sketch, "E35.11.2", {"start": v(5.72, -24.75) * mm, "end": v(5.37, -27.42) * mm});
            skLineSegment(sketch, "E35.11.3", {"start": v(5.5, -21.78) * mm, "end": v(5.72, -24.75) * mm});
            skLineSegment(sketch, "E35.12.0", {"start": v(8.34, -20.85) * mm, "end": v(9.92, -23.38) * mm});
            skLineSegment(sketch, "E35.12.1", {"start": v(9.92, -23.38) * mm, "end": v(11.77, -25.34) * mm});
            skLineSegment(sketch, "E35.12.2", {"start": v(13.09, -21.77) * mm, "end": v(13.58, -24.42) * mm});
            skLineSegment(sketch, "E35.12.3", {"start": v(11.97, -19) * mm, "end": v(13.09, -21.77) * mm});
            skLineSegment(sketch, "E35.13.0", {"start": v(14.38, -17.25) * mm, "end": v(16.66, -19.17) * mm});
            skLineSegment(sketch, "E35.13.1", {"start": v(16.66, -19.17) * mm, "end": v(19.03, -20.46) * mm});
            skLineSegment(sketch, "E35.13.2", {"start": v(19.17, -16.66) * mm, "end": v(20.46, -19.03) * mm});
            skLineSegment(sketch, "E35.13.3", {"start": v(17.25, -14.38) * mm, "end": v(19.17, -16.66) * mm});
            skLineSegment(sketch, "E35.14.0", {"start": v(19, -11.97) * mm, "end": v(21.77, -13.09) * mm});
            skLineSegment(sketch, "E35.14.1", {"start": v(21.77, -13.09) * mm, "end": v(24.42, -13.58) * mm});
            skLineSegment(sketch, "E35.14.2", {"start": v(23.38, -9.92) * mm, "end": v(25.34, -11.77) * mm});
            skLineSegment(sketch, "E35.14.3", {"start": v(20.85, -8.34) * mm, "end": v(23.38, -9.92) * mm});
            skLineSegment(sketch, "E35.15.0", {"start": v(21.78, -5.5) * mm, "end": v(24.75, -5.72) * mm});
            skLineSegment(sketch, "E35.15.1", {"start": v(24.75, -5.72) * mm, "end": v(27.42, -5.37) * mm});
            skLineSegment(sketch, "E35.15.2", {"start": v(25.3, -2.2) * mm, "end": v(27.74, -3.36) * mm});
            skLineSegment(sketch, "E35.15.3", {"start": v(22.41, -1.5) * mm, "end": v(25.3, -2.2) * mm});
            skLineSegment(sketch, "E35.16.0", {"start": v(22.41, 1.5) * mm, "end": v(25.3, 2.2) * mm});
            skLineSegment(sketch, "E35.16.1", {"start": v(25.3, 2.2) * mm, "end": v(27.74, 3.36) * mm});
            skLineSegment(sketch, "E35.16.2", {"start": v(24.75, 5.72) * mm, "end": v(27.42, 5.37) * mm});
            skLineSegment(sketch, "E35.16.3", {"start": v(21.78, 5.5) * mm, "end": v(24.75, 5.72) * mm});
            skLineSegment(sketch, "E35.17.0", {"start": v(20.85, 8.34) * mm, "end": v(23.38, 9.92) * mm});
            skLineSegment(sketch, "E35.17.1", {"start": v(23.38, 9.92) * mm, "end": v(25.34, 11.77) * mm});
            skLineSegment(sketch, "E35.17.2", {"start": v(21.77, 13.09) * mm, "end": v(24.42, 13.58) * mm});
            skLineSegment(sketch, "E35.17.3", {"start": v(19, 11.97) * mm, "end": v(21.77, 13.09) * mm});
            skLineSegment(sketch, "E35.18.0", {"start": v(17.25, 14.38) * mm, "end": v(19.17, 16.66) * mm});
            skLineSegment(sketch, "E35.18.1", {"start": v(19.17, 16.66) * mm, "end": v(20.46, 19.03) * mm});
            skLineSegment(sketch, "E35.18.2", {"start": v(16.66, 19.17) * mm, "end": v(19.03, 20.46) * mm});
            skLineSegment(sketch, "E35.18.3", {"start": v(14.38, 17.25) * mm, "end": v(16.66, 19.17) * mm});
            skLineSegment(sketch, "E35.19.0", {"start": v(11.97, 19) * mm, "end": v(13.09, 21.77) * mm});
            skLineSegment(sketch, "E35.19.1", {"start": v(13.09, 21.77) * mm, "end": v(13.58, 24.42) * mm});
            skLineSegment(sketch, "E35.19.2", {"start": v(9.92, 23.38) * mm, "end": v(11.77, 25.34) * mm});
            skLineSegment(sketch, "E35.19.3", {"start": v(8.34, 20.85) * mm, "end": v(9.92, 23.38) * mm});
            skSolve(sketch);
        }
        {
            var Q0;
            {var subQ48=sQuery(id+"F2.wireOp",EDGE,"E16");var subQ74=makeQuery(id+"F2.imprint","INTERSECT",VERTEX,{"derivedFrom":[subQ48,sQuery(id+"F2.wireOp",EDGE,"E25.5.1")]});Q0=makeQuery(id+"F2.imprint","IMPRINT",FACE,{"disambiguationData":[TD([[makeQuery(id+"F2.imprint","IMPRINT",EDGE,{"disambiguationData":[TD([[subQ74,1.0]])],"derivedFrom":subQ48}),-1.0]])]});}
            var Q1;
            {var subQ0=sQuery(id+"F2.wireOp",EDGE,"E35.3.2");Q1=makeQuery(id+"F2.imprint","IMPRINT",FACE,{"disambiguationData":[TD([[makeQuery(id+"F2.imprint","IMPRINT",EDGE,{"derivedFrom":subQ0}),1.0]])]});}
            var Q2;
            {var subQ1=sQuery(id+"F2.wireOp",EDGE,"E35.2.2");Q2=makeQuery(id+"F2.imprint","IMPRINT",FACE,{"disambiguationData":[TD([[makeQuery(id+"F2.imprint","IMPRINT",EDGE,{"derivedFrom":subQ1}),1.0]])]});}
            var Q3;
            {var subQ0=sQuery(id+"F2.wireOp",EDGE,"E35.1.2");Q3=makeQuery(id+"F2.imprint","IMPRINT",FACE,{"disambiguationData":[TD([[makeQuery(id+"F2.imprint","IMPRINT",EDGE,{"derivedFrom":subQ0}),1.0]])]});}
            var Q4;
            {var subQ1=sQuery(id+"F2.wireOp",EDGE,"E29");Q4=makeQuery(id+"F2.imprint","IMPRINT",FACE,{"disambiguationData":[TD([[makeQuery(id+"F2.imprint","IMPRINT",EDGE,{"derivedFrom":subQ1}),1.0]])]});}
            var Q5;
            {var subQ1=sQuery(id+"F2.wireOp",EDGE,"E31");Q5=makeQuery(id+"F2.imprint","IMPRINT",FACE,{"disambiguationData":[TD([[makeQuery(id+"F2.imprint","IMPRINT",EDGE,{"derivedFrom":subQ1}),-1.0]])]});}
            var Q6;
            {var subQ3=sQuery(id+"F2.wireOp",EDGE,"E35.18.2");Q6=makeQuery(id+"F2.imprint","IMPRINT",FACE,{"disambiguationData":[TD([[makeQuery(id+"F2.imprint","IMPRINT",EDGE,{"derivedFrom":subQ3}),1.0]])]});}
            var Q7;
            {var subQ1=sQuery(id+"F2.wireOp",EDGE,"E35.17.2");Q7=makeQuery(id+"F2.imprint","IMPRINT",FACE,{"disambiguationData":[TD([[makeQuery(id+"F2.imprint","IMPRINT",EDGE,{"derivedFrom":subQ1}),1.0]])]});}
            var Q8;
            {var subQ1=sQuery(id+"F2.wireOp",EDGE,"E35.16.2");Q8=makeQuery(id+"F2.imprint","IMPRINT",FACE,{"disambiguationData":[TD([[makeQuery(id+"F2.imprint","IMPRINT",EDGE,{"derivedFrom":subQ1}),1.0]])]});}
            var Q9;
            {var subQ1=sQuery(id+"F2.wireOp",EDGE,"E35.15.2");Q9=makeQuery(id+"F2.imprint","IMPRINT",FACE,{"disambiguationData":[TD([[makeQuery(id+"F2.imprint","IMPRINT",EDGE,{"derivedFrom":subQ1}),1.0]])]});}
            var Q10;
            {var subQ1=sQuery(id+"F2.wireOp",EDGE,"E35.14.2");Q10=makeQuery(id+"F2.imprint","IMPRINT",FACE,{"disambiguationData":[TD([[makeQuery(id+"F2.imprint","IMPRINT",EDGE,{"derivedFrom":subQ1}),1.0]])]});}
            var Q11;
            {var subQ3=sQuery(id+"F2.wireOp",EDGE,"E35.13.2");Q11=makeQuery(id+"F2.imprint","IMPRINT",FACE,{"disambiguationData":[TD([[makeQuery(id+"F2.imprint","IMPRINT",EDGE,{"derivedFrom":subQ3}),1.0]])]});}
            var Q12;
            {var subQ0=sQuery(id+"F2.wireOp",EDGE,"E35.12.2");Q12=makeQuery(id+"F2.imprint","IMPRINT",FACE,{"disambiguationData":[TD([[makeQuery(id+"F2.imprint","IMPRINT",EDGE,{"derivedFrom":subQ0}),1.0]])]});}
            var Q13;
            {var subQ1=sQuery(id+"F2.wireOp",EDGE,"E35.11.2");Q13=makeQuery(id+"F2.imprint","IMPRINT",FACE,{"disambiguationData":[TD([[makeQuery(id+"F2.imprint","IMPRINT",EDGE,{"derivedFrom":subQ1}),1.0]])]});}
            var Q14;
            {var subQ0=sQuery(id+"F2.wireOp",EDGE,"E35.10.2");Q14=makeQuery(id+"F2.imprint","IMPRINT",FACE,{"disambiguationData":[TD([[makeQuery(id+"F2.imprint","IMPRINT",EDGE,{"derivedFrom":subQ0}),1.0]])]});}
            var Q15;
            {var subQ0=sQuery(id+"F2.wireOp",EDGE,"E35.11.0");Q15=makeQuery(id+"F2.imprint","IMPRINT",FACE,{"disambiguationData":[TD([[makeQuery(id+"F2.imprint","IMPRINT",EDGE,{"derivedFrom":subQ0}),-1.0]])]});}
            var Q16;
            {var subQ1=sQuery(id+"F2.wireOp",EDGE,"E35.9.2");Q16=makeQuery(id+"F2.imprint","IMPRINT",FACE,{"disambiguationData":[TD([[makeQuery(id+"F2.imprint","IMPRINT",EDGE,{"derivedFrom":subQ1}),1.0]])]});}
            var Q17;
            {var subQ1=sQuery(id+"F2.wireOp",EDGE,"E35.8.2");Q17=makeQuery(id+"F2.imprint","IMPRINT",FACE,{"disambiguationData":[TD([[makeQuery(id+"F2.imprint","IMPRINT",EDGE,{"derivedFrom":subQ1}),1.0]])]});}
            var Q18;
            {var subQ1=sQuery(id+"F2.wireOp",EDGE,"E35.7.2");Q18=makeQuery(id+"F2.imprint","IMPRINT",FACE,{"disambiguationData":[TD([[makeQuery(id+"F2.imprint","IMPRINT",EDGE,{"derivedFrom":subQ1}),1.0]])]});}
            var Q19;
            {var subQ1=sQuery(id+"F2.wireOp",EDGE,"E35.6.2");Q19=makeQuery(id+"F2.imprint","IMPRINT",FACE,{"disambiguationData":[TD([[makeQuery(id+"F2.imprint","IMPRINT",EDGE,{"derivedFrom":subQ1}),1.0]])]});}
            var Q20;
            {var subQ1=sQuery(id+"F2.wireOp",EDGE,"E35.5.2");Q20=makeQuery(id+"F2.imprint","IMPRINT",FACE,{"disambiguationData":[TD([[makeQuery(id+"F2.imprint","IMPRINT",EDGE,{"derivedFrom":subQ1}),1.0]])]});}
            var Q21;
            {var subQ2=sQuery(id+"F2.wireOp",EDGE,"E35.4.2");Q21=makeQuery(id+"F2.imprint","IMPRINT",FACE,{"disambiguationData":[TD([[makeQuery(id+"F2.imprint","IMPRINT",EDGE,{"derivedFrom":subQ2}),1.0]])]});}
            var Q22;
            {var subQ17=sQuery(id+"F2.wireOp",EDGE,"E27");var subQ62=makeQuery(id+"F2.imprint","INTERSECT",VERTEX,{"derivedFrom":[subQ17,sQuery(id+"F2.wireOp",EDGE,"E35.16.1")]});Q22=makeQuery(id+"F2.imprint","IMPRINT",FACE,{"disambiguationData":[TD([[makeQuery(id+"F2.imprint","IMPRINT",EDGE,{"disambiguationData":[TD([[subQ62,-1.0]])],"derivedFrom":subQ17}),-1.0]])]});}
            extrude(context, id + "F3", {"entities" : qUnion([Q0, Q1, Q2, Q3, Q4, Q5, Q6, Q7, Q8, Q9, Q10, Q11, Q12, Q13, Q14, Q15, Q16, Q17, Q18, Q19, Q20, Q21, Q22]), "operationType" : NewBodyOperationType.REMOVE, "oppositeDirection" : true, "depth" : 15.88 * mm});
        }
        {
            var Q0;
            Q0=makeQuery(id+"F1.opRevolve","SWEPT_FACE",FACE,{"disambiguationData":[OSD([sQuery(id+"F0.wireOp",EDGE,"E4")])]});
            extrude(context, id + "F4", {"entities" : qUnion([Q0]), "operationType" : NewBodyOperationType.REMOVE, "oppositeDirection" : true, "depth" : 0.25 * mm});
        }
    });
